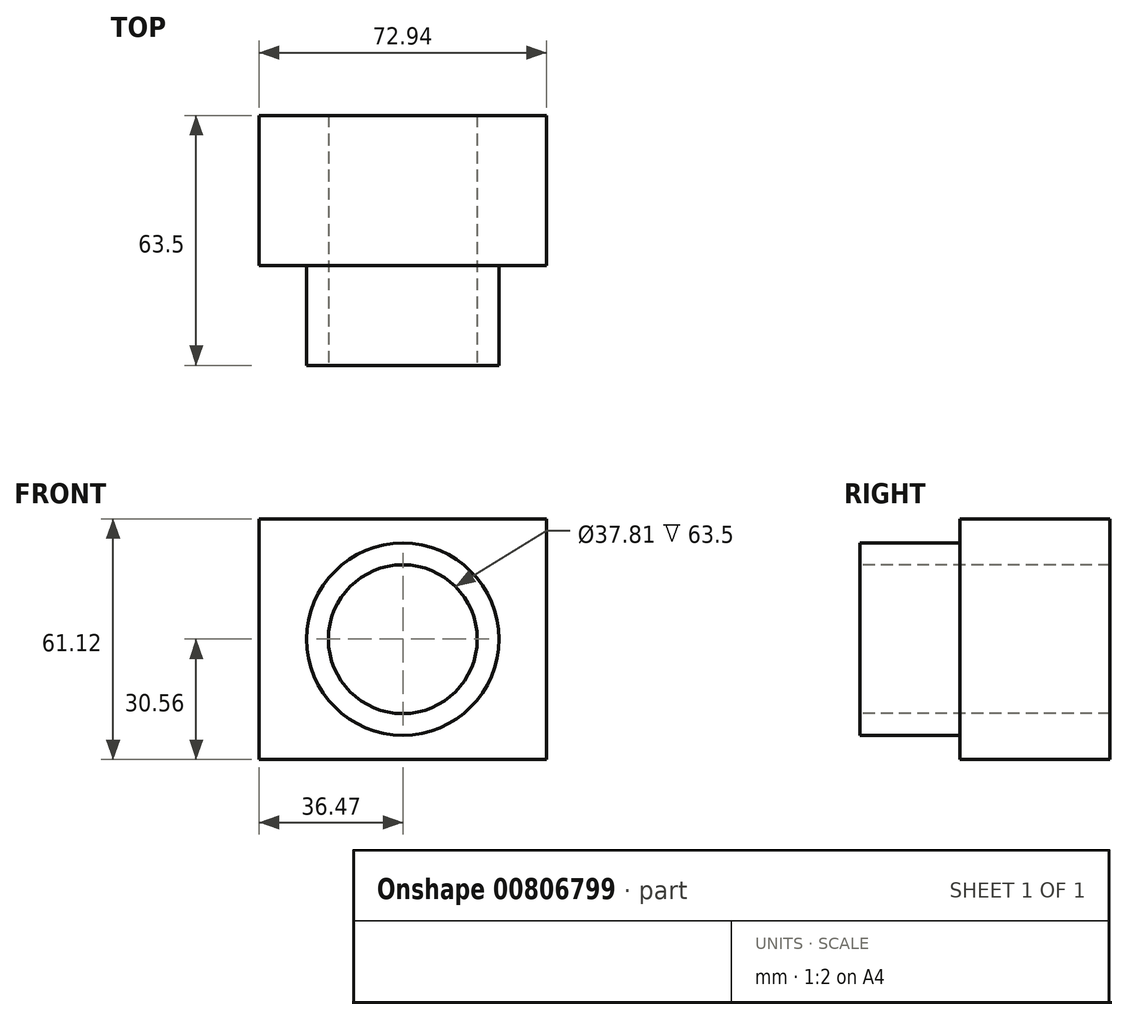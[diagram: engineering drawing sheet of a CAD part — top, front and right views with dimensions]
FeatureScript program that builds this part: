
annotation { "Feature Type Name" : "Feature", "Feature Type Description" : "" }
export const myFeature = defineFeature(function(context is Context, id is Id, definition is map)
    precondition{}
    {
        {
            var Q0;
            Q0=qCreatedBy(makeId("Front.planeOp"),FACE);
            var sketch = newSketch(context, id + "F0", { "sketchPlane" : qUnion([Q0])});
            skLineSegment(sketch, "E0.bottom", {"start": v(-36.47, 30.56) * mm, "end": v(36.47, 30.56) * mm});
            skLineSegment(sketch, "E0.top", {"start": v(-36.47, -30.56) * mm, "end": v(36.47, -30.56) * mm});
            skLineSegment(sketch, "E0.left", {"start": v(-36.47, 30.56) * mm, "end": v(-36.47, -30.56) * mm});
            skLineSegment(sketch, "E0.right", {"start": v(36.47, 30.56) * mm, "end": v(36.47, -30.56) * mm});
            skPoint(sketch, "E0.middle", {"position": v(0, 0) * mm});
            skSolve(sketch);
        }
        {
            var Q0;
            Q0=makeQuery(id+"F0.imprint","IMPRINT",FACE,{"disambiguationData":[TD([[makeQuery(id+"F0.imprint","IMPRINT",EDGE,{"derivedFrom":sQuery(id+"F0.wireOp",EDGE,"E0.bottom")}),-1.0]])]});
            extrude(context, id + "F1", {"entities" : qUnion([Q0]), "depth" : 38.1 * mm, "offsetDistance" : 25.4 * mm});
        }
        {
            var Q0;
            Q0=makeQuery(id+"F1.opExtrude","CAP_FACE",FACE,{"disambiguationData":[OSD([sQuery(id+"F0.wireOp",EDGE,"E0.bottom"),sQuery(id+"F0.wireOp",EDGE,"E0.top"),sQuery(id+"F0.wireOp",EDGE,"E0.left"),sQuery(id+"F0.wireOp",EDGE,"E0.right")])],"isStart":false});
            var sketch = newSketch(context, id + "F2", { "sketchPlane" : qUnion([Q0])});
            skCircle(sketch, "E1", {"center": v(0, 0) * mm, "radius": 24.13 * mm});
            skCircle(sketch, "E2", {"center": v(0, 0) * mm, "radius": 18.9 * mm});
            skSolve(sketch);
        }
        {
            var Q0;
            Q0=makeQuery(id+"F2.imprint","IMPRINT",FACE,{"disambiguationData":[TD([[makeQuery(id+"F2.imprint","IMPRINT",EDGE,{"derivedFrom":sQuery(id+"F2.wireOp",EDGE,"E2")}),1.0]])]});
            extrude(context, id + "F3", {"entities" : qUnion([Q0]), "operationType" : NewBodyOperationType.REMOVE, "oppositeDirection" : true, "depth" : 50.8 * mm, "offsetDistance" : 25.4 * mm});
        }
        {
            var Q0;
            Q0=makeQuery(id+"F1.opExtrude","CAP_FACE",FACE,{"disambiguationData":[OSD([sQuery(id+"F0.wireOp",EDGE,"E0.bottom"),sQuery(id+"F0.wireOp",EDGE,"E0.top"),sQuery(id+"F0.wireOp",EDGE,"E0.left"),sQuery(id+"F0.wireOp",EDGE,"E0.right")])],"isStart":false});
            var sketch = newSketch(context, id + "F4", { "sketchPlane" : qUnion([Q0])});
            skCircle(sketch, "E3", {"center": v(0, 0) * mm, "radius": 24.41 * mm});
            skSolve(sketch);
        }
        {
            var Q0;
            Q0=makeQuery(id+"F4.imprint","IMPRINT",FACE,{"disambiguationData":[TD([[makeQuery(id+"F4.imprint","IMPRINT",EDGE,{"derivedFrom":sQuery(id+"F4.wireOp",EDGE,"E3")}),1.0]])]});
            extrude(context, id + "F5", {"entities" : qUnion([Q0]), "operationType" : NewBodyOperationType.ADD, "depth" : 25.4 * mm, "offsetDistance" : 25.4 * mm});
        }
    });
